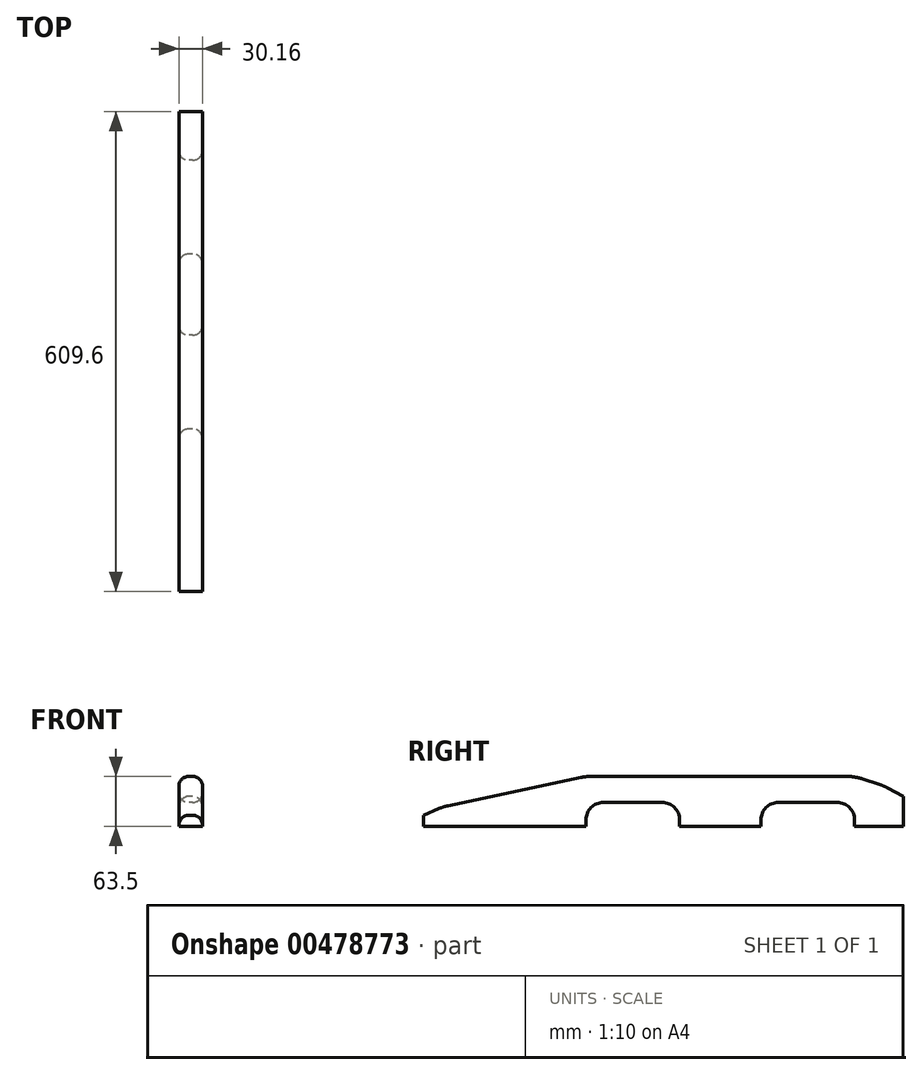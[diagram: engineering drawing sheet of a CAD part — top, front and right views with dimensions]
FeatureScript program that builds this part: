
annotation { "Feature Type Name" : "Feature", "Feature Type Description" : "" }
export const myFeature = defineFeature(function(context is Context, id is Id, definition is map)
    precondition{}
    {
        {
            var Q0;
            Q0=qCreatedBy(makeId("Right.planeOp"),FACE);
            var sketch = newSketch(context, id + "F0", { "sketchPlane" : qUnion([Q0])});
            skLineSegment(sketch, "E0.bottom", {"start": v(0, 0) * mm, "end": v(206.38, 0) * mm});
            skLineSegment(sketch, "E0.top", {"start": v(206.38, 63.5) * mm, "end": v(547.69, 63.5) * mm});
            skLineSegment(sketch, "E0.left", {"start": v(0, 0) * mm, "end": v(0, 14.29) * mm});
            skLineSegment(sketch, "E0.right", {"start": v(609.6, 0) * mm, "end": v(609.6, 38.1) * mm});
            skPoint(sketch, "E1", {"position": v(206.38, 0) * mm});
            skPoint(sketch, "E2", {"position": v(547.69, 0) * mm});
            skPoint(sketch, "E3", {"position": v(609.6, 38.1) * mm});
            skPoint(sketch, "E4", {"position": v(0, 14.29) * mm});
            skLineSegment(sketch, "E5", {"start": v(206.38, 0) * mm, "end": v(206.38, 30.48) * mm});
            skLineSegment(sketch, "E6", {"start": v(206.38, 30.48) * mm, "end": v(325.44, 30.48) * mm});
            skLineSegment(sketch, "E7", {"start": v(547.69, 30.48) * mm, "end": v(547.69, 0) * mm});
            skLineSegment(sketch, "E8.trimOffspring", {"start": v(547.69, 0) * mm, "end": v(609.6, 0) * mm});
            skLineSegment(sketch, "E9", {"start": v(0, 14.29) * mm, "end": v(25.4, 25.07) * mm});
            skLineSegment(sketch, "E10", {"start": v(25.4, 25.07) * mm, "end": v(206.38, 63.5) * mm});
            skLineSegment(sketch, "E11", {"start": v(609.6, 38.1) * mm, "end": v(584.2, 51.6) * mm});
            skLineSegment(sketch, "E12", {"start": v(584.2, 51.6) * mm, "end": v(547.69, 63.5) * mm});
            skLineSegment(sketch, "E13", {"start": v(325.44, 0) * mm, "end": v(428.62, 0) * mm});
            skLineSegment(sketch, "E14", {"start": v(325.44, 0) * mm, "end": v(325.44, 30.48) * mm});
            skLineSegment(sketch, "E15", {"start": v(428.62, 0) * mm, "end": v(428.62, 30.48) * mm});
            skLineSegment(sketch, "E16.trimOffspring", {"start": v(428.62, 30.48) * mm, "end": v(547.69, 30.48) * mm});
            skSolve(sketch);
        }
        {
            var Q0;
            Q0=makeQuery(id+"F0.imprint","IMPRINT",FACE,{"disambiguationData":[TD([[makeQuery(id+"F0.imprint","IMPRINT",EDGE,{"derivedFrom":sQuery(id+"F0.wireOp",EDGE,"E0.bottom")}),1.0]])]});
            extrude(context, id + "F1", {"entities" : qUnion([Q0]), "depth" : 15.08 * mm, "hasSecondDirection" : true, "secondDirectionOppositeDirection" : true, "secondDirectionDepth" : 15.08 * mm});
        }
        {
            var Q0;
            Q0=makeQuery(id+"F1.opExtrude","SWEPT_EDGE",EDGE,{"disambiguationData":[OSD([sQuery(id+"F0.wireOp",EDGE,"E9"),sQuery(id+"F0.wireOp",EDGE,"E10")])]});
            var Q1;
            Q1=makeQuery(id+"F1.opExtrude","SWEPT_EDGE",EDGE,{"disambiguationData":[OSD([sQuery(id+"F0.wireOp",EDGE,"E0.top"),sQuery(id+"F0.wireOp",EDGE,"E10")])]});
            var Q2;
            Q2=makeQuery(id+"F1.opExtrude","SWEPT_EDGE",EDGE,{"disambiguationData":[OSD([sQuery(id+"F0.wireOp",EDGE,"E0.top"),sQuery(id+"F0.wireOp",EDGE,"E12")])]});
            var Q3;
            Q3=makeQuery(id+"F1.opExtrude","SWEPT_EDGE",EDGE,{"disambiguationData":[OSD([sQuery(id+"F0.wireOp",EDGE,"E11"),sQuery(id+"F0.wireOp",EDGE,"E12")])]});
            fillet(context, id + "F2", {"entities" : qUnion([Q0, Q1, Q2, Q3]), "radius" : 63.5 * mm, "tangentPropagation" : true, "allowEdgeOverflow" : false});
        }
        {
            var Q0;
            Q0=makeQuery(id+"F1.opExtrude","SWEPT_EDGE",EDGE,{"disambiguationData":[OSD([sQuery(id+"F0.wireOp",EDGE,"E5"),sQuery(id+"F0.wireOp",EDGE,"E6")])]});
            var Q1;
            Q1=makeQuery(id+"F1.opExtrude","SWEPT_EDGE",EDGE,{"disambiguationData":[OSD([sQuery(id+"F0.wireOp",EDGE,"E6"),sQuery(id+"F0.wireOp",EDGE,"E14")])]});
            var Q2;
            Q2=makeQuery(id+"F1.opExtrude","SWEPT_EDGE",EDGE,{"disambiguationData":[OSD([sQuery(id+"F0.wireOp",EDGE,"E15"),sQuery(id+"F0.wireOp",EDGE,"E16.trimOffspring")])]});
            var Q3;
            Q3=makeQuery(id+"F1.opExtrude","SWEPT_EDGE",EDGE,{"disambiguationData":[OSD([sQuery(id+"F0.wireOp",EDGE,"E7"),sQuery(id+"F0.wireOp",EDGE,"E16.trimOffspring")])]});
            fillet(context, id + "F3", {"entities" : qUnion([Q0, Q1, Q2, Q3]), "radius" : 22.22 * mm, "tangentPropagation" : true, "allowEdgeOverflow" : false});
        }
        {
            var Q0;
            Q0=makeQuery(id+"F1.opExtrude","CAP_EDGE",EDGE,{"disambiguationData":[OSD([sQuery(id+"F0.wireOp",EDGE,"E6")])],"isStart":false});
            var Q1;
            Q1=makeQuery(id+"F1.opExtrude","CAP_EDGE",EDGE,{"disambiguationData":[OSD([sQuery(id+"F0.wireOp",EDGE,"E6")])],"isStart":true});
            var Q2;
            Q2=makeQuery(id+"F1.opExtrude","CAP_EDGE",EDGE,{"disambiguationData":[OSD([sQuery(id+"F0.wireOp",EDGE,"E16.trimOffspring")])],"isStart":false});
            var Q3;
            Q3=makeQuery(id+"F1.opExtrude","CAP_EDGE",EDGE,{"disambiguationData":[OSD([sQuery(id+"F0.wireOp",EDGE,"E16.trimOffspring")])],"isStart":true});
            var Q4;
            Q4=makeQuery(id+"F1.opExtrude","CAP_EDGE",EDGE,{"disambiguationData":[OSD([sQuery(id+"F0.wireOp",EDGE,"E0.top")])],"isStart":false});
            var Q5;
            Q5=makeQuery(id+"F1.opExtrude","CAP_EDGE",EDGE,{"disambiguationData":[OSD([sQuery(id+"F0.wireOp",EDGE,"E0.top")])],"isStart":true});
            fillet(context, id + "F4", {"entities" : qUnion([Q0, Q1, Q2, Q3, Q4, Q5]), "radius" : 12.7 * mm, "tangentPropagation" : true, "allowEdgeOverflow" : false});
        }
    });
